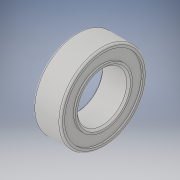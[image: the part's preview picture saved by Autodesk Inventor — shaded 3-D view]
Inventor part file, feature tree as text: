
AUTODESK INVENTOR PART (.ipt)
format: ipt  version: 2017 (Build 210142000, 142)  size: 163,328 bytes
history: native  units: in
note: dims shown in document units (in); Inventor stores cm internally (conversion verified against a paired STEP export)
features: revolve x1
ambient origin geometry x8: Origin, YZ Plane, XZ Plane, XY Plane, X Axis, Y Axis, Z Axis, Center Point
bodies: Solid1 (feature_tree)
feature tree (1):
  revolve  "Revolve1"  [1 undecoded]
note: 1 required parameter value undecoded (feature->parameter linkage not recoverable at this tier; creation-order binding heuristic only, values carry confidence <= 0.55)
